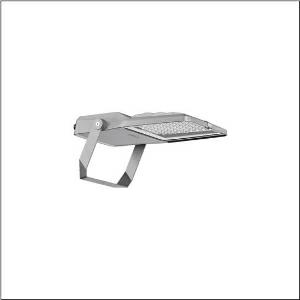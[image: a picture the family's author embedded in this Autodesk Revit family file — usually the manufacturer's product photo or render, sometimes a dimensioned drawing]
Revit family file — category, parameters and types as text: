
# Revit family: floodlight_fl_21_mini___pl64_5xa7772c1e1a_7520
name_source: partatom
category: Lighting Fixtures
units: mm (PartAtom-declared; Revit-internal decimal feet)

## family parameters
Cut with Voids When Loaded = No
Host = Face
Light Source = No
Part Type = Normal
Room Calculation Point = No
Round Connector Dimension = Use Diameter
Shared = No

## types (1)
- --- (1 x LED, 9770 lm, 87.2 W, 2200K)
    Apparent Load = 87 VA
    CIE Flux Codes = 28 80 98 100 100
    Color Rendering = 70
    Color Temperature = 2200K
    Default Elevation = 1800 mm
    Description = Floodlight FL 21 mini, floodlight, primary light control with lens, of PMMA, primary optical cover: protective disc, of toughened safety glass, transparent, light distribution: PL64, light emission: direct distribution, installation type: surface-mounted, LED, High Power LED, rated luminous flux: 9.770lm, luminous efficacy: 112lm/W, light colour: 722, colour temperature: 2200K, control gear: ECG iQ, control: Street-Remote, Auto-Match, Temp-Guard, Night-Set, Smart-Wire, Desk-Remote (wireless, voltage-free reading and setting of iQ features in the workshop via application-optimized NFC function/RFID function), optimised constant luminous flux control (CLO 2.0), with terminal, 6-pole, mains connection: 220..240V, AC, 50/60Hz, start of lifetime: 87W, end of lifetime: 92W, reduction: 40W, luminaire housing, of diecast aluminium, powder-coated, Siteco® metallic grey (DB 702S), corrosivity category C5 according to DIN EN ISO 12944, mounting bracket, of steel, galvanised, powder-coated, Siteco® metallic grey (DB 702S), protection rating (complete): IP66, insulation class (complete): insulation class II (safety insulation), certification: CE, ENEC, VDE, protection symbol: D, impact resistance: IK08, permissible operating ambient temperature: -40..+40°C, permissible operating ambient temperature for outdoor applications: -40..+50°C, standard: DIN EN 12944, packaging unit: 1 piece

Light Distribution: PL64
    Height = 70 mm
    Lamp = 1 x LED
    Lamp Light Flux = 9770 lm
    Lamp Power = 87.2 W
    Lamp count = 1
    Length = 485 mm
    Luminous efficacy = 112 lm/W
    Manufacturer = Siteco
    ModVariant = No
    Model = 5XA7772C1E1A
    Number of Poles = 1
    OnlyDefault = Yes
    Power Factor = 1
    Product Name = Floodlight FL 21 mini | PL64
    Product group = floodlight | pylon top
    ProductGroupID = 6101
    Protection Class = Protection class II
    Protection Degree = IP 66
    RLX_Detail_Level = 1
    RlxData = <blob elided: 96085 chars, md5=7e788dcb>
    Socket = socket
    Standby Power = 0 W
    System Light Flux = 9770 lm
    System Power = 87 W
    Type Comments = factory setting: luminous flux: 100 % | dim-lin: 254 | 456 mA
    Type Image = l_1006845.jpg
    URL = http://relux.com
    VarID = @adj_077521
    Voltage = 0 V
    Weight = 0.00 kg
    Width = 337 mm

## geometry (parser evidence)
native form markers: Blend x4, Sweep x14
no freeform markers — native parametric forms only
